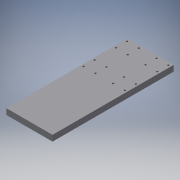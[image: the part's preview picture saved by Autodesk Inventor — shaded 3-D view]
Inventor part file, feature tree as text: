
AUTODESK INVENTOR PART (.ipt)
format: ipt  version: 2018 (Build 220112000, 112)  size: 127,488 bytes
history: native  units: mm
features: other x1, extrude x1, hole x1, sketch x1
ambient origin geometry x8: Origin, YZ Plane, XZ Plane, XY Plane, X Axis, Y Axis, Z Axis, Center Point
bodies: Body1 (feature_tree)
feature tree (4):
  other  "Sólido1"
  extrude  "Extrusão1"  Depth=328.47mm
  hole  "Furo1"  [1 undecoded]
  sketch  "Esboço3"  dims[d0=125.0mm d1=328.47mm d3=0.0mm d4=5.0mm d5=6.0mm d6=8.0mm d7=6.0mm d8=90.0deg d9=8.0mm d10=20.594885mm]
note: 1 required parameter value undecoded (feature->parameter linkage not recoverable at this tier; creation-order binding heuristic only, values carry confidence <= 0.55)
